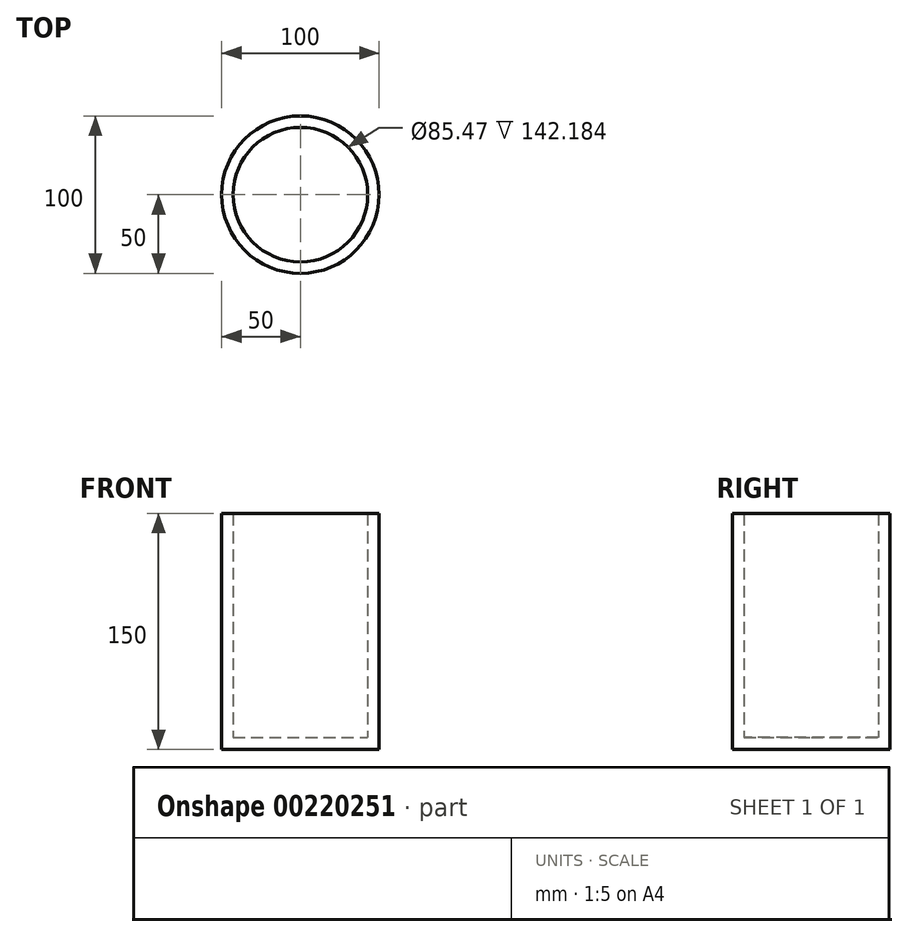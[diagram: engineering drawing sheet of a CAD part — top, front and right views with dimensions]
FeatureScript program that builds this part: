
annotation { "Feature Type Name" : "Feature", "Feature Type Description" : "" }
export const myFeature = defineFeature(function(context is Context, id is Id, definition is map)
    precondition{}
    {
        {
            var Q0;
            Q0=qCreatedBy(makeId("Front.planeOp"),FACE);
            var sketch = newSketch(context, id + "F0", { "sketchPlane" : qUnion([Q0])});
            skLineSegment(sketch, "E0", {"start": v(0, 0) * mm, "end": v(-50, 0) * mm});
            skLineSegment(sketch, "E1", {"start": v(-50, 0) * mm, "end": v(-50, 150) * mm});
            skLineSegment(sketch, "E2", {"start": v(0, -61.4) * mm, "end": v(0, 166.93) * mm});
            skLineSegment(sketch, "E3", {"start": v(-42.73, 150) * mm, "end": v(-42.73, 7.82) * mm});
            skLineSegment(sketch, "E4", {"start": v(-42.73, 7.82) * mm, "end": v(0, 7.82) * mm});
            skLineSegment(sketch, "E5", {"start": v(0, 7.82) * mm, "end": v(0, 0) * mm});
            skLineSegment(sketch, "E6", {"start": v(-50, 150) * mm, "end": v(-42.73, 150) * mm});
            skLineSegment(sketch, "E7", {"start": v(-50, 0) * mm, "end": v(0, 0) * mm});
            skSolve(sketch);
        }
        {
            var Q0;
            Q0=makeQuery(id+"F0.imprint","IMPRINT",FACE,{"disambiguationData":[TD([[makeQuery(id+"F0.imprint","IMPRINT",EDGE,{"derivedFrom":sQuery(id+"F0.wireOp",EDGE,"E1")}),-1.0]])]});
            var Q1;
            Q1=sQuery(id+"F0.wireOp",EDGE,"E2");
            revolve(context, id + "F1", {"entities" : qUnion([Q0]), "axis" : qUnion([Q1]), "revolveType" : RevolveType.FULL});
        }
    });
